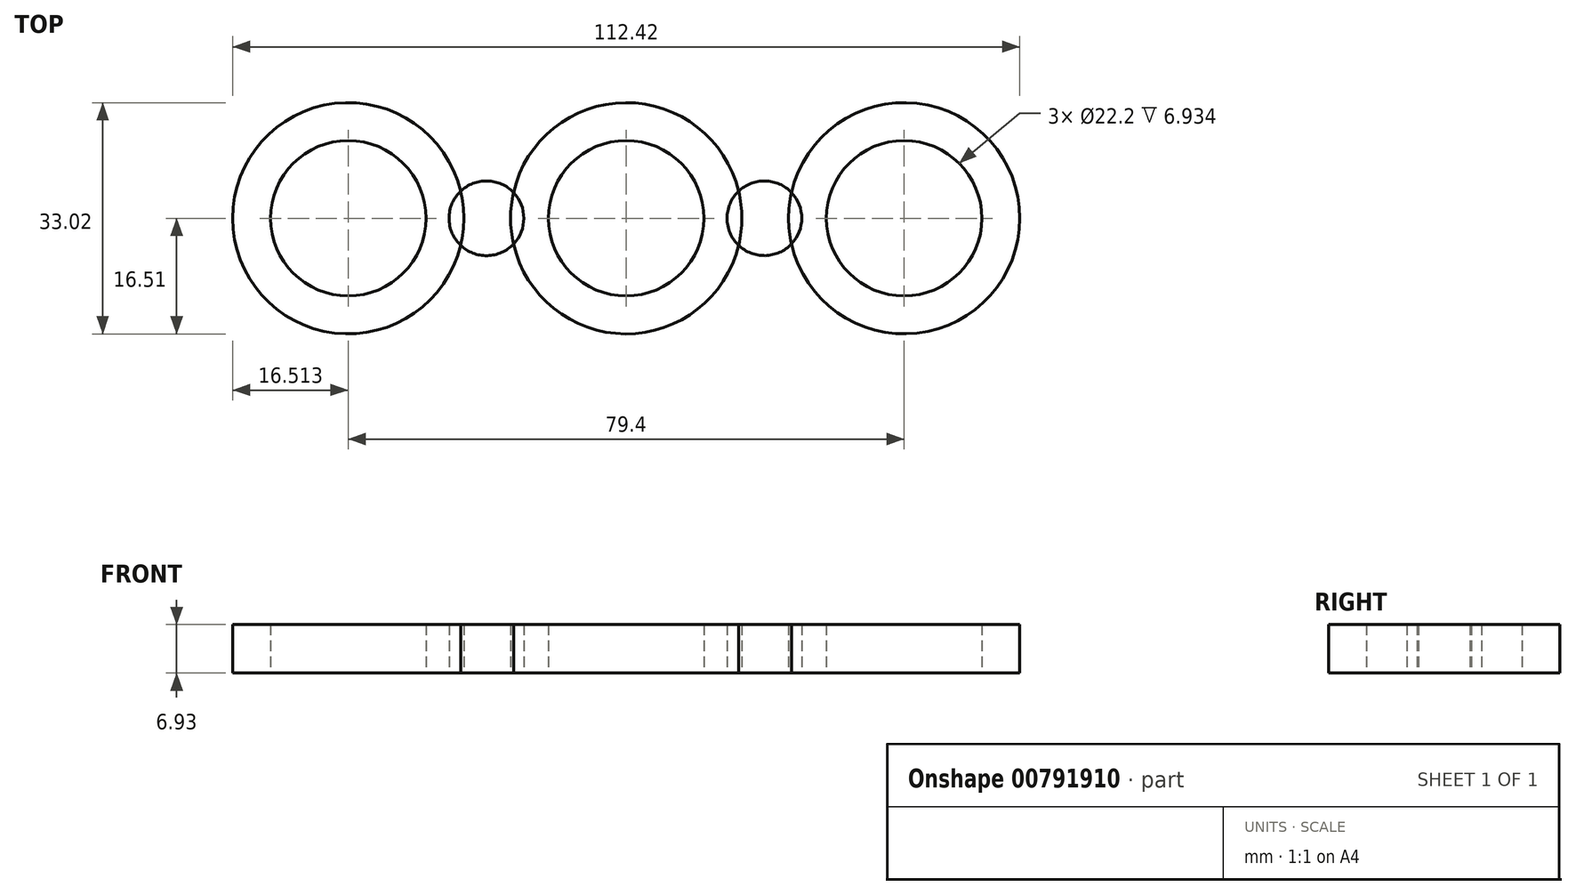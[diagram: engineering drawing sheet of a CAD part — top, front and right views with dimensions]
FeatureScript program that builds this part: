
annotation { "Feature Type Name" : "Feature", "Feature Type Description" : "" }
export const myFeature = defineFeature(function(context is Context, id is Id, definition is map)
    precondition{}
    {
        {
            var Q0;
            Q0=qCreatedBy(makeId("Top.planeOp"),FACE);
            var sketch = newSketch(context, id + "F0", { "sketchPlane" : qUnion([Q0])});
            skCircle(sketch, "E0", {"center": v(-75.28, 0) * mm, "radius": 11.1 * mm});
            skCircle(sketch, "E1", {"center": v(-35.58, 0) * mm, "radius": 11.1 * mm});
            skCircle(sketch, "E2", {"center": v(4.12, 0) * mm, "radius": 11.1 * mm});
            skCircle(sketch, "E3", {"center": v(4.12, 0) * mm, "radius": 16.51 * mm});
            skCircle(sketch, "E4", {"center": v(-35.58, 0) * mm, "radius": 16.51 * mm});
            skCircle(sketch, "E5", {"center": v(-75.28, 0) * mm, "radius": 16.51 * mm});
            skCircle(sketch, "E6", {"center": v(-55.54, 0) * mm, "radius": 5.34 * mm});
            skCircle(sketch, "E7", {"center": v(-15.84, 0) * mm, "radius": 5.33 * mm});
            skSolve(sketch);
        }
        {
            var Q0;
            Q0=makeQuery(id+"F0.imprint","IMPRINT",FACE,{"disambiguationData":[TD([[makeQuery(id+"F0.imprint","IMPRINT",EDGE,{"derivedFrom":sQuery(id+"F0.wireOp",EDGE,"E0")}),-1.0]])]});
            var Q1;
            {var subQ0=sQuery(id+"F0.wireOp",EDGE,"E6");var subQ1=sQuery(id+"F0.wireOp",EDGE,"E4");var subQ2=makeQuery(id+"F0.imprint","INTERSECT",VERTEX,{"disambiguationData":[OD(0.0)],"derivedFrom":[subQ1,subQ0]});Q1=makeQuery(id+"F0.imprint","IMPRINT",FACE,{"disambiguationData":[TD([[makeQuery(id+"F0.imprint","IMPRINT",EDGE,{"disambiguationData":[TD([[subQ2,-1.0]])],"derivedFrom":subQ1}),-1.0]])]});}
            var Q2;
            Q2=makeQuery(id+"F0.imprint","IMPRINT",FACE,{"disambiguationData":[TD([[makeQuery(id+"F0.imprint","IMPRINT",EDGE,{"derivedFrom":sQuery(id+"F0.wireOp",EDGE,"E2")}),-1.0]])]});
            var Q3;
            Q3=makeQuery(id+"F0.imprint","IMPRINT",FACE,{"disambiguationData":[TD([[makeQuery(id+"F0.imprint","IMPRINT",EDGE,{"derivedFrom":sQuery(id+"F0.wireOp",EDGE,"E1")}),-1.0]])]});
            var Q4;
            {var subQ0=sQuery(id+"F0.wireOp",EDGE,"E7");var subQ1=sQuery(id+"F0.wireOp",EDGE,"E3");var subQ2=makeQuery(id+"F0.imprint","INTERSECT",VERTEX,{"disambiguationData":[OD(0.0)],"derivedFrom":[subQ1,subQ0]});Q4=makeQuery(id+"F0.imprint","IMPRINT",FACE,{"disambiguationData":[TD([[makeQuery(id+"F0.imprint","IMPRINT",EDGE,{"disambiguationData":[TD([[subQ2,-1.0]])],"derivedFrom":subQ1}),-1.0]])]});}
            extrude(context, id + "F1", {"entities" : qUnion([Q0, Q1, Q2, Q3, Q4]), "depth" : 6.93 * mm, "offsetDistance" : 25.4 * mm});
        }
    });
